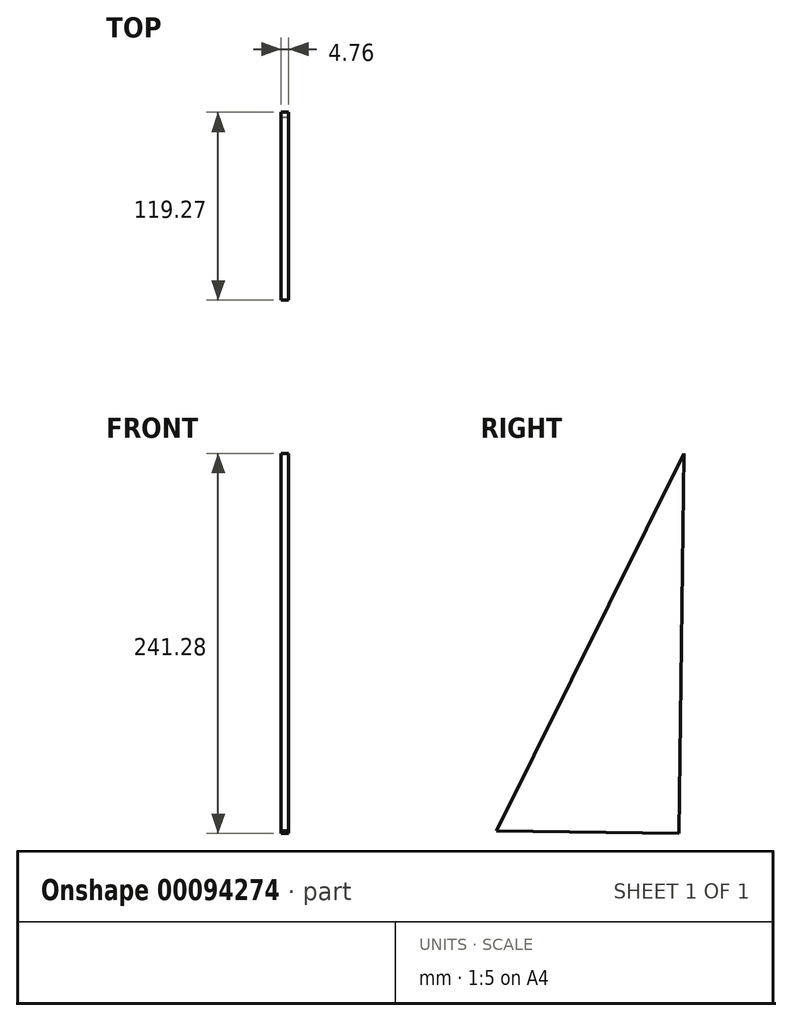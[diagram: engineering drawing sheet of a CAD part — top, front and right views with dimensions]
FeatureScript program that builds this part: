
annotation { "Feature Type Name" : "Feature", "Feature Type Description" : "" }
export const myFeature = defineFeature(function(context is Context, id is Id, definition is map)
    precondition{}
    {
        {
            var Q0;
            Q0=qCreatedBy(makeId("Right.planeOp"),FACE);
            var sketch = newSketch(context, id + "F0", { "sketchPlane" : qUnion([Q0])});
            skLineSegment(sketch, "E0.bottom", {"start": v(0, 0) * mm, "end": v(-115.81, 1.66) * mm});
            skLineSegment(sketch, "E0.left", {"start": v(0, 0) * mm, "end": v(3.46, 241.28) * mm});
            skLineSegment(sketch, "E1", {"start": v(-115.81, 1.66) * mm, "end": v(3.46, 241.28) * mm});
            skSolve(sketch);
        }
        {
            var Q0;
            Q0=makeQuery(id+"F0.imprint","IMPRINT",FACE,{"disambiguationData":[TD([[makeQuery(id+"F0.imprint","IMPRINT",EDGE,{"derivedFrom":sQuery(id+"F0.wireOp",EDGE,"E0.bottom")}),-1.0]])]});
            extrude(context, id + "F1", {"entities" : qUnion([Q0]), "depth" : 4.76 * mm});
        }
    });
